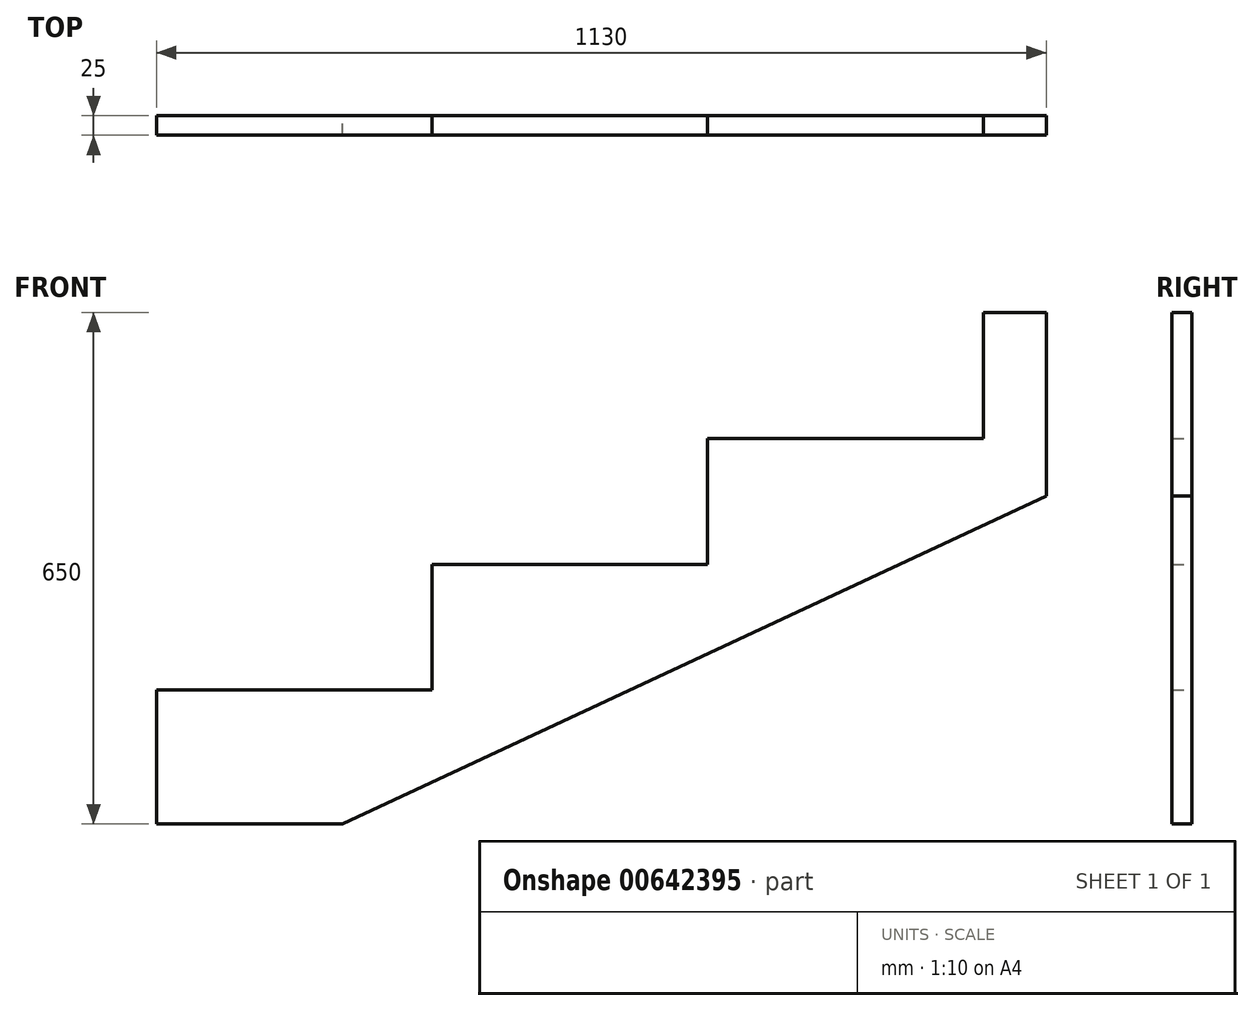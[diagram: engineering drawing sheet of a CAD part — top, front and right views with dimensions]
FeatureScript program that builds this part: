
annotation { "Feature Type Name" : "Feature", "Feature Type Description" : "" }
export const myFeature = defineFeature(function(context is Context, id is Id, definition is map)
    precondition{}
    {
        {
            var Q0;
            Q0=qCreatedBy(makeId("Front.planeOp"),FACE);
            var sketch = newSketch(context, id + "F0", { "sketchPlane" : qUnion([Q0])});
            skLineSegment(sketch, "E0", {"start": v(0, 650) * mm, "end": v(-80, 650) * mm});
            skLineSegment(sketch, "E1", {"start": v(-80, 650) * mm, "end": v(-80, 490) * mm});
            skLineSegment(sketch, "E2", {"start": v(-80, 490) * mm, "end": v(-430, 490) * mm});
            skLineSegment(sketch, "E3", {"start": v(-430, 490) * mm, "end": v(-430, 330) * mm});
            skLineSegment(sketch, "E4", {"start": v(-430, 330) * mm, "end": v(-780, 330) * mm});
            skLineSegment(sketch, "E5", {"start": v(-780, 330) * mm, "end": v(-780, 170) * mm});
            skLineSegment(sketch, "E6", {"start": v(-780, 170) * mm, "end": v(-1130, 170) * mm});
            skLineSegment(sketch, "E7", {"start": v(-1130, 170) * mm, "end": v(-1130, 0) * mm});
            skLineSegment(sketch, "E8", {"start": v(-1130, 0) * mm, "end": v(-893.53, 0) * mm});
            skLineSegment(sketch, "E9", {"start": v(-80, 490) * mm, "end": v(-1130, 0) * mm, "construction": true});
            skLineSegment(sketch, "E10", {"start": v(-893.53, 0) * mm, "end": v(0, 416.98) * mm});
            skLineSegment(sketch, "E11", {"start": v(-893.53, 0) * mm, "end": v(0, 0) * mm, "construction": true});
            skLineSegment(sketch, "E12", {"start": v(0, 650) * mm, "end": v(0, 416.98) * mm});
            skLineSegment(sketch, "E13", {"start": v(0, 416.98) * mm, "end": v(0, 0) * mm, "construction": true});
            skSolve(sketch);
        }
        {
            var Q0;
            Q0 = qSketchRegion(id + "F0", true);
            extrude(context, id + "F1", {"entities" : qUnion([Q0]), "depth" : 25 * mm, "offsetDistance" : 25 * mm});
        }
    });
